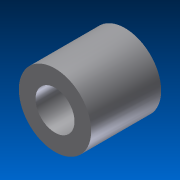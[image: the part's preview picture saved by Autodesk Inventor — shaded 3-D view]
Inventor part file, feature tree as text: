
AUTODESK INVENTOR PART (.ipt)
format: ipt  version: 2012 (Build 160160000, 160)  size: 81,408 bytes
history: native  units: in
note: dims shown in document units (in); Inventor stores cm internally (conversion verified against a paired STEP export)
features: extrude x1, sketch x1
ambient origin geometry x8: Origin, YZ Plane, XZ Plane, XY Plane, X Axis, Y Axis, Z Axis, Center Point
bodies: Solid1 (feature_tree)
feature tree (2):
  extrude  "Extrusion1"  Depth=0.1709in
  sketch  "Sketch1"  dims[d0=0.0921in d1=0.1709in d2=0.1654in d3=0.0in]
